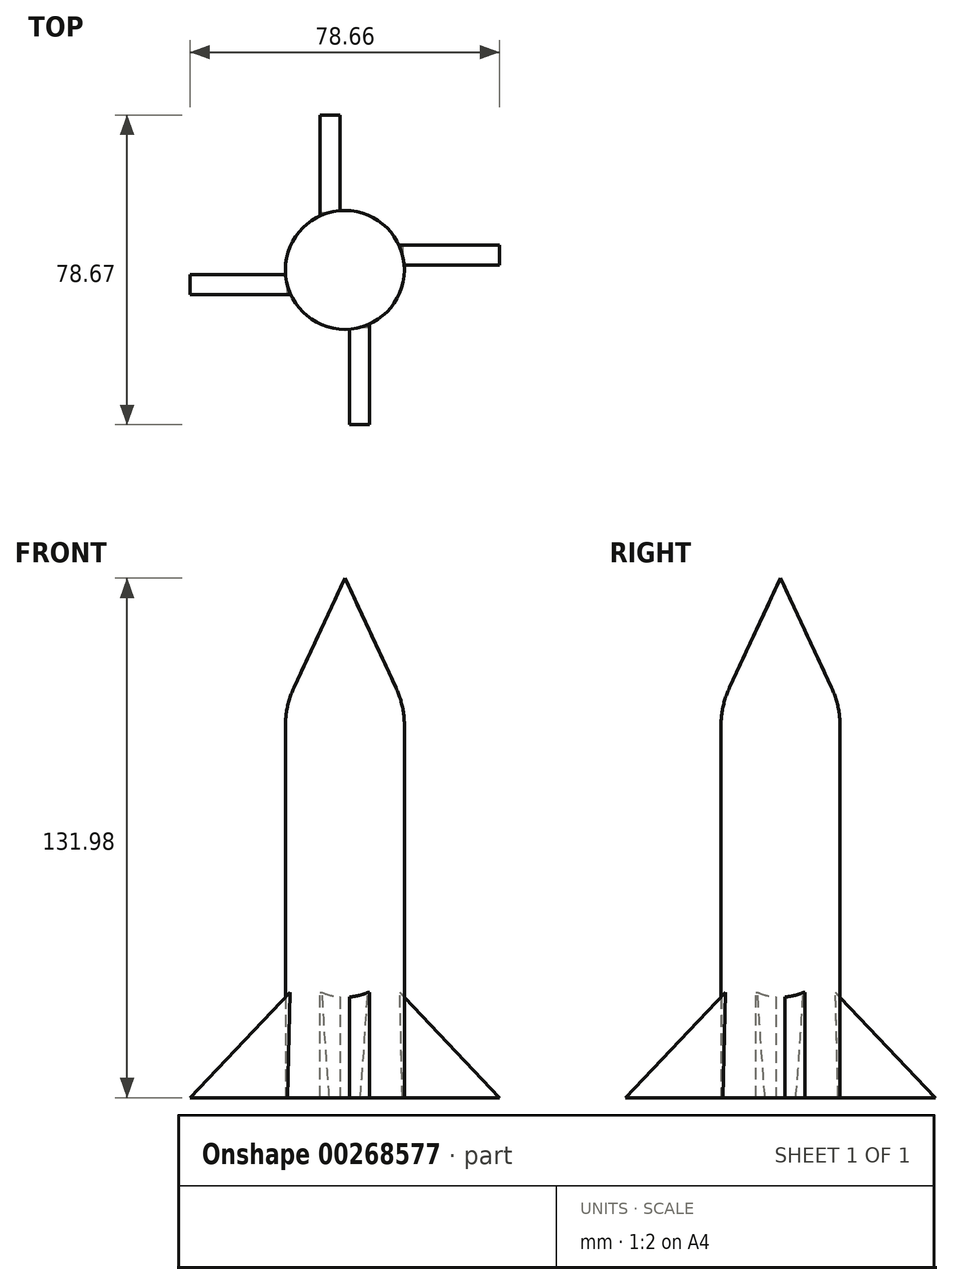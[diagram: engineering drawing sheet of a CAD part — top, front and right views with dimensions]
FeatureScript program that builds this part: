
annotation { "Feature Type Name" : "Feature", "Feature Type Description" : "" }
export const myFeature = defineFeature(function(context is Context, id is Id, definition is map)
    precondition{}
    {
        {
            var Q0;
            Q0=qCreatedBy(makeId("Top.planeOp"),FACE);
            var sketch = newSketch(context, id + "F0", { "sketchPlane" : qUnion([Q0])});
            skCircle(sketch, "E0", {"center": v(0, 3.72) * mm, "radius": 15.11 * mm});
            skSolve(sketch);
        }
        {
            var Q0;
            Q0=makeQuery(id+"F0.imprint","IMPRINT",FACE,{"disambiguationData":[TD([[makeQuery(id+"F0.imprint","IMPRINT",EDGE,{"derivedFrom":sQuery(id+"F0.wireOp",EDGE,"E0")}),1.0]])]});
            extrude(context, id + "F1", {"entities" : qUnion([Q0]), "depth" : 99.57 * mm});
        }
        {
            var Q0;
            Q0=makeQuery(id+"F1.opExtrude","CAP_FACE",FACE,{"disambiguationData":[OSD([sQuery(id+"F0.wireOp",EDGE,"E0")])],"isStart":false});
            extrude(context, id + "F2", {"entities" : qUnion([Q0]), "operationType" : NewBodyOperationType.ADD, "depth" : 54.86 * mm, "hasDraft" : true, "draftAngle" : 25 * degree, "draftPullDirection" : true});
        }
        {
            var Q0;
            {var subQ0=sQuery(id+"F0.wireOp",EDGE,"E0");Q0=makeQuery(id+"F2.boolean.opBoolean","MERGE",EDGE,{"derivedFrom":[makeQuery(id+"F1.opExtrude","CAP_EDGE",EDGE,{"disambiguationData":[OSD([subQ0])],"isStart":false}),makeQuery(id+"F2.opExtrude","CAP_EDGE",EDGE,{"disambiguationData":[OSD([subQ0])],"isStart":true})]});}
            fillet(context, id + "F3", {"entities" : qUnion([Q0]), "radius" : 22.86 * mm, "tangentPropagation" : true, "allowEdgeOverflow" : false});
        }
        {
            var Q0;
            Q0=qCreatedBy(makeId("Front.planeOp"),FACE);
            var sketch = newSketch(context, id + "F4", { "sketchPlane" : qUnion([Q0])});
            skLineSegment(sketch, "E1", {"start": v(-15.87, 17.5) * mm, "end": v(-32.56, 0) * mm});
            skLineSegment(sketch, "E2", {"start": v(-32.56, 0) * mm, "end": v(-15.47, 0) * mm});
            skLineSegment(sketch, "E3", {"start": v(-15.87, 17.5) * mm, "end": v(-15.47, 0) * mm});
            skSolve(sketch);
        }
        {
            var Q0;
            Q0 = qSketchRegion(id + "F4", true);
            extrude(context, id + "F5", {"entities" : qUnion([Q0]), "depth" : 3.3 * mm});
        }
        {
            var Q0;
            Q0=makeQuery(id+"F5.opExtrude","SWEPT_BODY",BODY,{"disambiguationData":[OSD([sQuery(id+"F4.wireOp",EDGE,"E1"),sQuery(id+"F4.wireOp",EDGE,"E2"),sQuery(id+"F4.wireOp",EDGE,"E3")])]});
            deleteBodies(context, id + "F6", {"entities" : qUnion([Q0])});
        }
        {
            var Q0;
            Q0=qCreatedBy(makeId("Front.planeOp"),FACE);
            var sketch = newSketch(context, id + "F7", { "sketchPlane" : qUnion([Q0])});
            skLineSegment(sketch, "E4", {"start": v(-13.97, 26.73) * mm, "end": v(-39.33, 0) * mm});
            skLineSegment(sketch, "E5", {"start": v(-39.33, 0) * mm, "end": v(-14.6, 0) * mm});
            skLineSegment(sketch, "E6", {"start": v(-14.6, 0) * mm, "end": v(-13.97, 26.73) * mm});
            skSolve(sketch);
        }
        {
            var Q0;
            Q0 = qSketchRegion(id + "F7", true);
            extrude(context, id + "F8", {"entities" : qUnion([Q0]), "operationType" : NewBodyOperationType.ADD, "endBound" : BoundingType.SYMMETRIC, "depth" : 5.08 * mm});
        }
        {
            var Q0;
            Q0=makeQuery(id+"F1.opExtrude","SWEPT_BODY",BODY,{"disambiguationData":[OSD([sQuery(id+"F0.wireOp",EDGE,"E0")])]});
            var Q1;
            Q1=makeQuery(id+"F2.opExtrude","SWEPT_FACE",FACE,{"disambiguationData":[OSD([sQuery(id+"F0.wireOp",EDGE,"E0")])]});
            circularPattern(context, id + "F9", {"entities" : qUnion([Q0]), "axis" : qUnion([Q1]), "angle" : 360 * degree, "instanceCount" : 4, "equalSpace" : true});
        }
        {
            var Q0;
            Q0=makeQuery(id+"F8.boolean.opBoolean","MERGE",FACE,{"derivedFrom":[makeQuery(id+"F1.opExtrude","CAP_FACE",FACE,{"disambiguationData":[OSD([sQuery(id+"F0.wireOp",EDGE,"E0")])],"isStart":true}),makeQuery(id+"F8.opExtrude","SWEPT_FACE",FACE,{"disambiguationData":[OSD([sQuery(id+"F7.wireOp",EDGE,"E5")])]})]});
            shell(context, id + "F10", {"entities" : qUnion([Q0]), "thickness" : 2.54 * mm});
        }
        {
            var Q0;
            Q0=makeQuery(id+"F9.opPattern","COPY",FACE,{"derivedFrom":makeQuery(id+"F8.boolean.opBoolean","MERGE",FACE,{"derivedFrom":[makeQuery(id+"F1.opExtrude","CAP_FACE",FACE,{"disambiguationData":[OSD([sQuery(id+"F0.wireOp",EDGE,"E0")])],"isStart":true}),makeQuery(id+"F8.opExtrude","SWEPT_FACE",FACE,{"disambiguationData":[OSD([sQuery(id+"F7.wireOp",EDGE,"E5")])]})]}),"instanceName":"1"});
            shell(context, id + "F11", {"entities" : qUnion([Q0]), "thickness" : 2.54 * mm});
        }
    });
